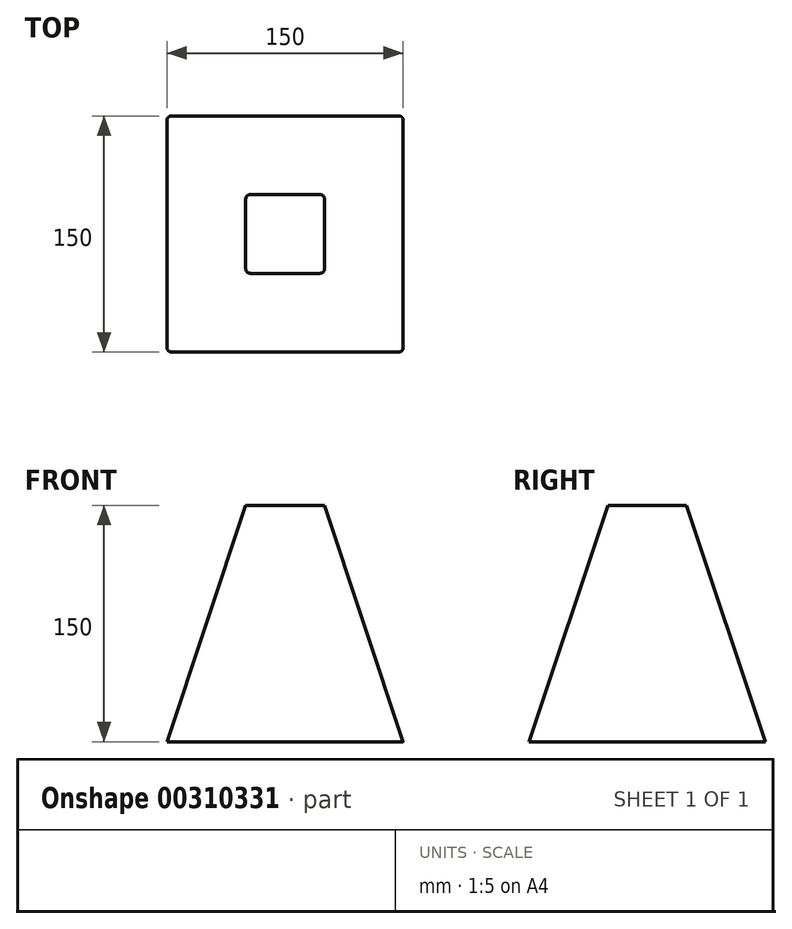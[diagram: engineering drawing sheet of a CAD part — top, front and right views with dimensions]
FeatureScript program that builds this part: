
annotation { "Feature Type Name" : "Feature", "Feature Type Description" : "" }
export const myFeature = defineFeature(function(context is Context, id is Id, definition is map)
    precondition{}
    {
        {
            var Q0;
            Q0=qCreatedBy(makeId("Top.planeOp"),FACE);
            var sketch = newSketch(context, id + "F0", { "sketchPlane" : qUnion([Q0])});
            skLineSegment(sketch, "E0.bottom", {"start": v(-75, 75) * mm, "end": v(75, 75) * mm});
            skLineSegment(sketch, "E0.top", {"start": v(-75, -75) * mm, "end": v(75, -75) * mm});
            skLineSegment(sketch, "E0.left", {"start": v(-75, 75) * mm, "end": v(-75, -75) * mm});
            skLineSegment(sketch, "E0.right", {"start": v(75, 75) * mm, "end": v(75, -75) * mm});
            skSolve(sketch);
        }
        {
            var Q0;
            Q0=makeQuery(id+"F0.imprint","IMPRINT",FACE,{"disambiguationData":[TD([[makeQuery(id+"F0.imprint","IMPRINT",EDGE,{"derivedFrom":sQuery(id+"F0.wireOp",EDGE,"E0.bottom")}),-1.0]])]});
            cPlane(context, id + "F1", {"entities" : qUnion([Q0]), "cplaneType" : CPlaneType.OFFSET, "offset" : 150 * mm, "width" : 150 * mm, "height" : 150 * mm});
        }
        {
            var Q0;
            Q0=qCreatedBy(id+"F1.planeOp",FACE);
            var sketch = newSketch(context, id + "F2", { "sketchPlane" : qUnion([Q0])});
            skLineSegment(sketch, "E1.bottom", {"start": v(-25, 25) * mm, "end": v(25, 25) * mm});
            skLineSegment(sketch, "E1.top", {"start": v(-25, -25) * mm, "end": v(25, -25) * mm});
            skLineSegment(sketch, "E1.left", {"start": v(-25, 25) * mm, "end": v(-25, -25) * mm});
            skLineSegment(sketch, "E1.right", {"start": v(25, 25) * mm, "end": v(25, -25) * mm});
            skSolve(sketch);
        }
        {
            var Q0;
            Q0=makeQuery(id+"F0.imprint","IMPRINT",FACE,{"disambiguationData":[TD([[makeQuery(id+"F0.imprint","IMPRINT",EDGE,{"derivedFrom":sQuery(id+"F0.wireOp",EDGE,"E0.bottom")}),-1.0]])]});
            var Q1;
            Q1=makeQuery(id+"F2.imprint","IMPRINT",FACE,{"disambiguationData":[TD([[makeQuery(id+"F2.imprint","IMPRINT",EDGE,{"derivedFrom":sQuery(id+"F2.wireOp",EDGE,"E1.bottom")}),-1.0]])]});
            loft(context, id + "F3", {"sheetProfilesArray" : [{ "sheetProfileEntities" : qUnion([Q0]) }, { "sheetProfileEntities" : qUnion([Q1]) }]});
        }
        {
            var Q0;
            Q0=makeQuery(id+"F3.opLoft","SWEPT_EDGE",EDGE,{"disambiguationData":[OSD([sQuery(id+"F0.wireOp",EDGE,"E0.top"),sQuery(id+"F0.wireOp",EDGE,"E0.right"),sQuery(id+"F2.wireOp",EDGE,"E1.top"),sQuery(id+"F2.wireOp",EDGE,"E1.right")])]});
            var Q1;
            Q1=makeQuery(id+"F3.opLoft","SWEPT_EDGE",EDGE,{"disambiguationData":[OSD([sQuery(id+"F0.wireOp",EDGE,"E0.top"),sQuery(id+"F0.wireOp",EDGE,"E0.left"),sQuery(id+"F2.wireOp",EDGE,"E1.top"),sQuery(id+"F2.wireOp",EDGE,"E1.left")])]});
            var Q2;
            Q2=makeQuery(id+"F3.opLoft","SWEPT_EDGE",EDGE,{"disambiguationData":[OSD([sQuery(id+"F0.wireOp",EDGE,"E0.bottom"),sQuery(id+"F0.wireOp",EDGE,"E0.right"),sQuery(id+"F2.wireOp",EDGE,"E1.bottom"),sQuery(id+"F2.wireOp",EDGE,"E1.right")])]});
            var Q3;
            Q3=makeQuery(id+"F3.opLoft","SWEPT_EDGE",EDGE,{"disambiguationData":[OSD([sQuery(id+"F0.wireOp",EDGE,"E0.bottom"),sQuery(id+"F0.wireOp",EDGE,"E0.left"),sQuery(id+"F2.wireOp",EDGE,"E1.bottom"),sQuery(id+"F2.wireOp",EDGE,"E1.left")])]});
            fillet(context, id + "F4", {"entities" : qUnion([Q0, Q1, Q2, Q3]), "radius" : 3 * mm, "tangentPropagation" : true, "allowEdgeOverflow" : false});
        }
    });
